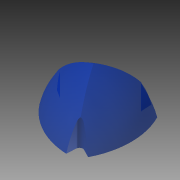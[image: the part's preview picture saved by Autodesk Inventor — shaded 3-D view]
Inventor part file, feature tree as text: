
AUTODESK INVENTOR PART (.ipt)
format: ipt  version: 2013 (Build 170138000, 138)  size: 126,976 bytes
history: native  units: mm
features: sketch x3, extrude x2, pattern_circular x2, revolve x1
ambient origin geometry x8: Origin, YZ Plane, XZ Plane, XY Plane, X Axis, Y Axis, Z Axis, Center Point
bodies: Solid1 (feature_tree)
feature tree (8):
  extrude  "Extrusion1"  Depth=1000.0mm TaperAngle=0.0deg
  revolve  "Revolution1"  [1 undecoded]
  pattern_circular  "Circular Pattern1"  Count=59  [1 undecoded]
  extrude  "Extrusion2"  Depth=912.511899mm
  pattern_circular  "Circular Pattern2"  Angle=90.0deg  [1 undecoded]
  sketch  "Sketch1"  dims[d0=1000.0mm d2=1000.0mm d3=0.0mm]
  sketch  "Sketch2"  dims[d4=250.0mm d5=72.0mm d6=590.0mm]
  sketch  "Sketch3"  dims[d7=1732.19184mm d8=912.511899mm d9=90.0deg d10=30.0mm d11=360.0deg d13=25.0mm d15=1000.0mm d16=0.0mm d17=30.0mm d18=360.0deg]
note: 3 required parameter values undecoded (feature->parameter linkage not recoverable at this tier; creation-order binding heuristic only, values carry confidence <= 0.55)